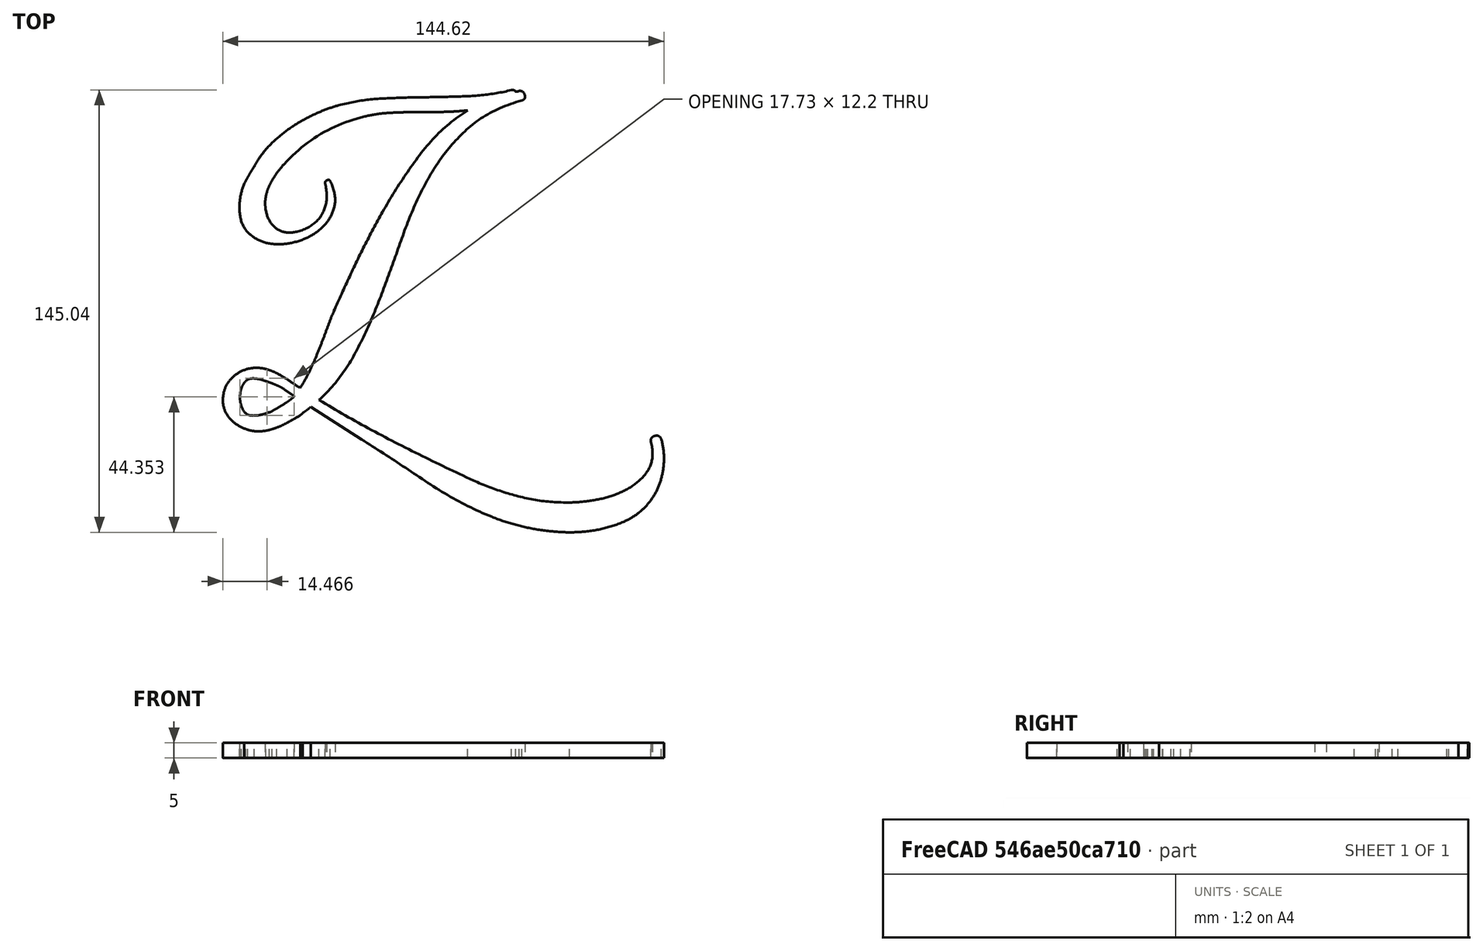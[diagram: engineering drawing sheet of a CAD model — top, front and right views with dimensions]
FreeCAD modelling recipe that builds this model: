
FCSTD DOCUMENT  (FreeCAD 1.0R39109 (Git))
Label: labrit
License: All rights reserved
LicenseURL: http://en.wikipedia.org/wiki/All_rights_reserved
objects: Part::Part2DObjectPython×1, Part::Extrusion×1
note: 2 computed .brp shape members not serialized (recipe doc carries the construction recipe); baked Part::Feature solids carry a one-line shape summary decoded from their .brp

FEATURE [Part::Part2DObjectPython] ShapeString  # Draft 2D object (typed FeaturePython)
  FontFile = <path> Rainbow Script FREE.ttf
  Fuse = false
  Justification = 6
  JustificationReference = 0
  KeepLeftMargin = true
  MakeFace = true
  ObliqueAngle = 0
  Placement = pos=(-2.3,0.7,0) rot=(0,0,1;0rad)
  ScaleToSize = false
  Size = 50
  String = L
  Tracking = 0
FEATURE [Part::Extrusion] Extrude
  Base = -> ShapeString
  Dir = (0,0,1)
  DirMode = 2
  FaceMakerClass = Part::FaceMakerBullseye
  FaceMakerMode = 3
  LengthFwd = 5
  LengthRev = 0
  Solid = false
  Symmetric = false
note: 1 file-system path scrubbed to <path> (originals preserved in the JSON sidecar)
